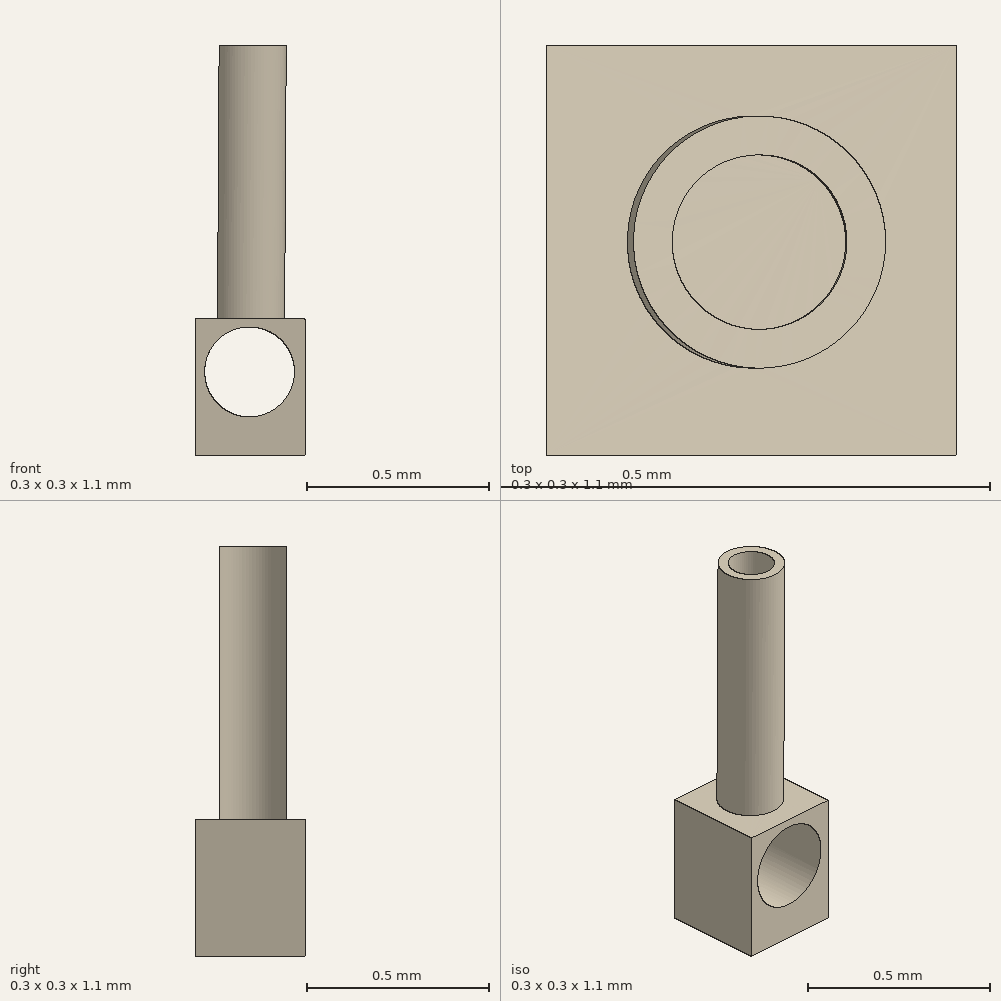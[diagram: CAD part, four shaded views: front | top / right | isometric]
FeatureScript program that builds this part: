
annotation { "Feature Type Name" : "Feature", "Feature Type Description" : "" }
export const myFeature = defineFeature(function(context is Context, id is Id, definition is map)
    precondition{}
    {
        {
            var Q0;
            Q0=qCreatedBy(makeId("Front.planeOp"),FACE);
            var sketch = newSketch(context, id + "F0", { "sketchPlane" : qUnion([Q0])});
            skLineSegment(sketch, "E0", {"start": v(0, 0.38) * mm, "end": v(0, 0) * mm});
            skLineSegment(sketch, "E1", {"start": v(0, 0) * mm, "end": v(0.3, 0) * mm});
            skLineSegment(sketch, "E2", {"start": v(0.3, 0) * mm, "end": v(0.3, 0.38) * mm});
            skLineSegment(sketch, "E3", {"start": v(0.3, 0.38) * mm, "end": v(0, 0.38) * mm});
            skSolve(sketch);
        }
        {
            var Q0;
            Q0=qCreatedBy(makeId("Front.planeOp"),FACE);
            var sketch = newSketch(context, id + "F1", { "sketchPlane" : qUnion([Q0])});
            skLineSegment(sketch, "E4", {"start": v(0, 0.38) * mm, "end": v(0, 0) * mm});
            skLineSegment(sketch, "E5", {"start": v(0, 0) * mm, "end": v(0.3, 0) * mm});
            skLineSegment(sketch, "E6", {"start": v(0.3, 0) * mm, "end": v(0.3, 0.38) * mm});
            skLineSegment(sketch, "E7", {"start": v(0.3, 0.38) * mm, "end": v(0, 0.38) * mm});
            skSolve(sketch);
        }
        {
            var Q0;
            Q0=makeQuery(id+"F0.imprint","IMPRINT",FACE,{"disambiguationData":[TD([[makeQuery(id+"F0.imprint","IMPRINT",EDGE,{"derivedFrom":sQuery(id+"F0.wireOp",EDGE,"E0")}),1.0]])]});
            extrude(context, id + "F2", {"entities" : qUnion([Q0]), "oppositeDirection" : true, "depth" : .300 * mm, "offsetDistance" : 25 * mm});
        }
        {
            var Q0;
            Q0=makeQuery(id+"F2.opExtrude","SWEPT_FACE",FACE,{"disambiguationData":[OSD([sQuery(id+"F0.wireOp",EDGE,"E3")])]});
            var sketch = newSketch(context, id + "F3", { "sketchPlane" : qUnion([Q0])});
            skCircle(sketch, "E8", {"center": v(0.15, 0.16) * mm, "radius": 0.1 * mm});
            skSolve(sketch);
        }
        {
            var Q0;
            Q0=makeQuery(id+"F3.imprint","IMPRINT",FACE,{"disambiguationData":[TD([[makeQuery(id+"F3.imprint","IMPRINT",EDGE,{"derivedFrom":sQuery(id+"F3.wireOp",EDGE,"E8")}),1.0]])]});
            extrude(context, id + "F4", {"entities" : qUnion([Q0]), "operationType" : NewBodyOperationType.ADD, "depth" : .75 * mm});
        }
        {
            var Q0;
            Q0=qCreatedBy(makeId("Front.planeOp"),FACE);
            var sketch = newSketch(context, id + "F5", { "sketchPlane" : qUnion([Q0])});
            skCircle(sketch, "E9", {"center": v(0.15, 0.23) * mm, "radius": 0.11 * mm});
            skSolve(sketch);
        }
        {
            var Q0;
            Q0 = qSketchRegion(id + "F5", true);
            extrude(context, id + "F6", {"entities" : qUnion([Q0]), "operationType" : NewBodyOperationType.REMOVE, "oppositeDirection" : true, "depth" : .300 * mm});
        }
        {
            var Q0;
            Q0=makeQuery(id+"F4.opExtrude","CAP_FACE",FACE,{"disambiguationData":[OSD([sQuery(id+"F3.wireOp",EDGE,"E8")])],"isStart":false});
            var sketch = newSketch(context, id + "F7", { "sketchPlane" : qUnion([Q0])});
            skCircle(sketch, "E10", {"center": v(0.15, 0.16) * mm, "radius": 0.06 * mm});
            skSolve(sketch);
        }
        {
            var Q0;
            Q0 = qSketchRegion(id + "F7", true);
            extrude(context, id + "F8", {"entities" : qUnion([Q0]), "operationType" : NewBodyOperationType.REMOVE, "oppositeDirection" : true, "depth" : .150 * mm});
        }
        {
            var Q0;
            Q0=makeQuery(id+"F1.imprint","IMPRINT",FACE,{"disambiguationData":[TD([[makeQuery(id+"F1.imprint","IMPRINT",EDGE,{"derivedFrom":sQuery(id+"F1.wireOp",EDGE,"E4")}),1.0]])]});
            var sketch = newSketch(context, id + "F9", { "sketchPlane" : qUnion([Q0])});
            skCircle(sketch, "E11", {"center": v(0.15, 0.23) * mm, "radius": 0.12 * mm});
            skSolve(sketch);
        }
        {
            var Q0;
            Q0=makeQuery(id+"F9.imprint","IMPRINT",FACE,{"disambiguationData":[TD([[makeQuery(id+"F9.imprint","IMPRINT",EDGE,{"derivedFrom":sQuery(id+"F9.wireOp",EDGE,"E11")}),1.0]])]});
            var Q1;
            Q1=sQuery(id+"F9.wireOp",EDGE,"E11");
            extrude(context, id + "F10", {"entities" : qUnion([Q0]), "operationType" : NewBodyOperationType.REMOVE, "surfaceEntities" : qUnion([Q1]), "oppositeDirection" : true, "depth" : .5 * mm});
        }
        {
            var Q0;
            Q0=makeQuery(id+"F2.opExtrude","CAP_FACE",FACE,{"disambiguationData":[OSD([sQuery(id+"F0.wireOp",EDGE,"E0"),sQuery(id+"F0.wireOp",EDGE,"E1"),sQuery(id+"F0.wireOp",EDGE,"E2"),sQuery(id+"F0.wireOp",EDGE,"E3")])],"isStart":false});
            var sketch = newSketch(context, id + "F11", { "sketchPlane" : qUnion([Q0])});
            skCircle(sketch, "E12", {"center": v(-0.15, 0.23) * mm, "radius": 0.12 * mm});
            skSolve(sketch);
        }
        {
            var Q0;
            Q0 = qSketchRegion(id + "F11", true);
            extrude(context, id + "F12", {"entities" : qUnion([Q0]), "operationType" : NewBodyOperationType.REMOVE, "oppositeDirection" : true, "depth" : 0.05 * mm});
        }
    });
